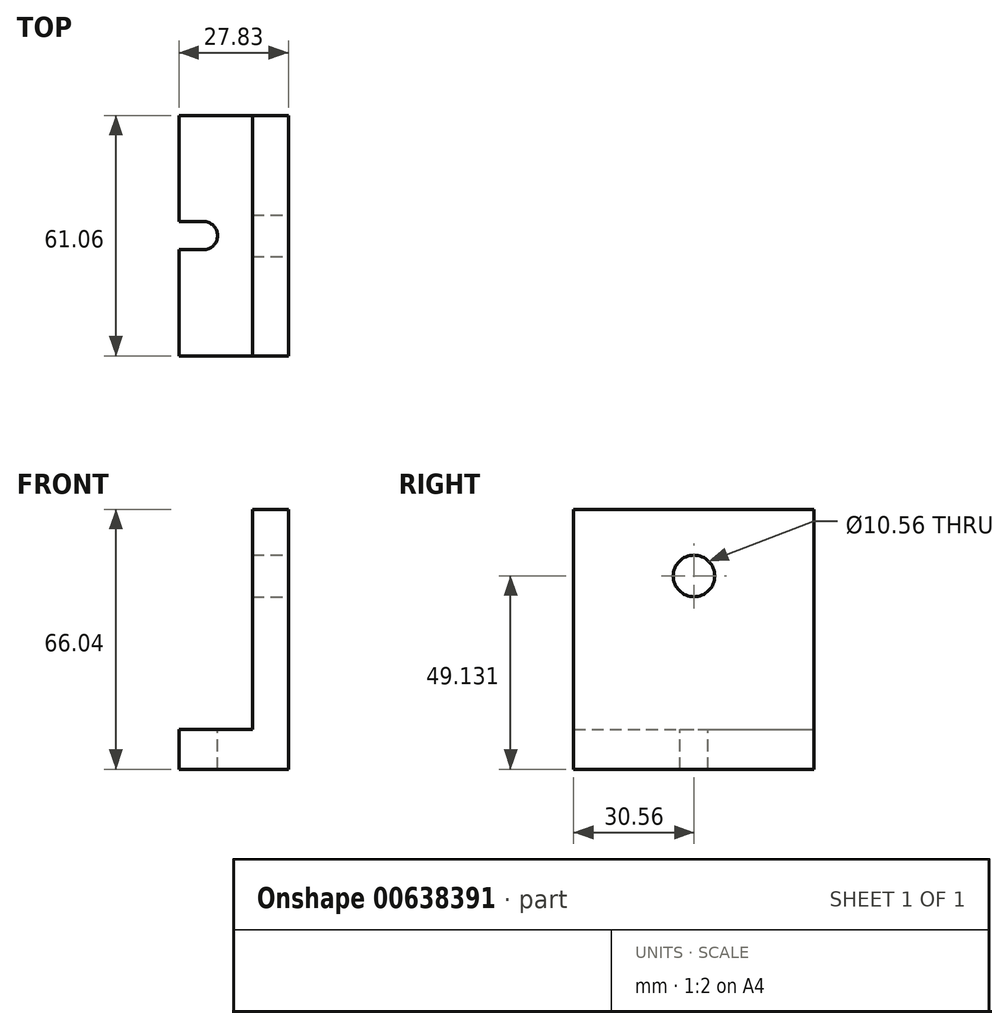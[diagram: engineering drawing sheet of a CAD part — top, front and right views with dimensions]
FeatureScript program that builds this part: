
annotation { "Feature Type Name" : "Feature", "Feature Type Description" : "" }
export const myFeature = defineFeature(function(context is Context, id is Id, definition is map)
    precondition{}
    {
        {
            var Q0;
            Q0=qCreatedBy(makeId("Top.planeOp"),FACE);
            var sketch = newSketch(context, id + "F0", { "sketchPlane" : qUnion([Q0])});
            skLineSegment(sketch, "E0.bottom", {"start": v(0, 0) * mm, "end": v(-18.7, 0) * mm});
            skLineSegment(sketch, "E0.top", {"start": v(0, 30.5) * mm, "end": v(-18.7, 30.5) * mm});
            skLineSegment(sketch, "E0.left", {"start": v(0, 0) * mm, "end": v(0, 30.5) * mm});
            skLineSegment(sketch, "E0.right", {"start": v(-18.7, 0) * mm, "end": v(-18.7, 30.5) * mm});
            skLineSegment(sketch, "E1.top", {"start": v(0, -30.56) * mm, "end": v(-18.7, -30.56) * mm});
            skLineSegment(sketch, "E1.left", {"start": v(0, 0) * mm, "end": v(0, -30.56) * mm});
            skLineSegment(sketch, "E1.right", {"start": v(-18.7, 0) * mm, "end": v(-18.7, -30.56) * mm});
            skLineSegment(sketch, "E2.bottom", {"start": v(0, 30.5) * mm, "end": v(9.13, 30.5) * mm});
            skLineSegment(sketch, "E2.top", {"start": v(0, -30.56) * mm, "end": v(9.13, -30.56) * mm});
            skLineSegment(sketch, "E2.left", {"start": v(0, 30.5) * mm, "end": v(0, -30.56) * mm});
            skLineSegment(sketch, "E2.right", {"start": v(9.13, 30.5) * mm, "end": v(9.13, -30.56) * mm});
            skSolve(sketch);
        }
        {
            var Q0;
            {var subQ3=sQuery(id+"F0.wireOp",EDGE,"E2.bottom");Q0=makeQuery(id+"F0.imprint","IMPRINT",FACE,{"disambiguationData":[TD([[makeQuery(id+"F0.imprint","IMPRINT",EDGE,{"derivedFrom":subQ3}),-1.0]])]});}
            extrude(context, id + "F1", {"entities" : qUnion([Q0]), "depth" : 66.04 * mm, "offsetDistance" : 25.4 * mm});
        }
        {
            var Q0;
            {var subQ0=sQuery(id+"F0.wireOp",EDGE,"E0.top");Q0=makeQuery(id+"F0.imprint","IMPRINT",FACE,{"disambiguationData":[TD([[makeQuery(id+"F0.imprint","IMPRINT",EDGE,{"derivedFrom":subQ0}),1.0]])]});}
            var Q1;
            {var subQ0=sQuery(id+"F0.wireOp",EDGE,"E0.bottom");Q1=makeQuery(id+"F0.imprint","IMPRINT",FACE,{"disambiguationData":[TD([[makeQuery(id+"F0.imprint","IMPRINT",EDGE,{"derivedFrom":subQ0}),1.0]])]});}
            extrude(context, id + "F2", {"entities" : qUnion([Q0, Q1]), "operationType" : NewBodyOperationType.ADD, "depth" : 10.16 * mm, "offsetDistance" : 25.4 * mm});
        }
        {
            var Q0;
            Q0=makeQuery(id+"F1.opExtrude","SWEPT_FACE",FACE,{"disambiguationData":[OSD([sQuery(id+"F0.wireOp",EDGE,"E2.right")])]});
            var sketch = newSketch(context, id + "F3", { "sketchPlane" : qUnion([Q0])});
            skCircle(sketch, "E3", {"center": v(0, 49.13) * mm, "radius": 5.28 * mm});
            skSolve(sketch);
        }
        {
            var Q0;
            Q0=makeQuery(id+"F3.imprint","IMPRINT",FACE,{"disambiguationData":[TD([[makeQuery(id+"F3.imprint","IMPRINT",EDGE,{"derivedFrom":sQuery(id+"F3.wireOp",EDGE,"E3")}),1.0]])]});
            extrude(context, id + "F4", {"entities" : qUnion([Q0]), "operationType" : NewBodyOperationType.REMOVE, "oppositeDirection" : true, "depth" : 25.4 * mm, "offsetDistance" : 25.4 * mm});
        }
        {
            var Q0;
            Q0=makeQuery(id+"F2.opExtrude","CAP_FACE",FACE,{"disambiguationData":[OSD([sQuery(id+"F0.wireOp",EDGE,"E0.top"),sQuery(id+"F0.wireOp",EDGE,"E0.right"),sQuery(id+"F0.wireOp",EDGE,"E1.top"),sQuery(id+"F0.wireOp",EDGE,"E1.right"),sQuery(id+"F0.wireOp",EDGE,"E2.left")])],"isStart":false});
            var sketch = newSketch(context, id + "F5", { "sketchPlane" : qUnion([Q0])});
            skCircle(sketch, "E4", {"center": v(-12.46, 0) * mm, "radius": 3.6 * mm});
            skLineSegment(sketch, "E5", {"start": v(-12.46, 0) * mm, "end": v(-12.46, 3.6) * mm});
            skLineSegment(sketch, "E6", {"start": v(-12.46, 0) * mm, "end": v(-12.46, -3.6) * mm});
            skLineSegment(sketch, "E7", {"start": v(-12.46, 3.6) * mm, "end": v(-18.7, 3.6) * mm});
            skLineSegment(sketch, "E8", {"start": v(-12.46, -3.6) * mm, "end": v(-19.35, -3.6) * mm});
            skSolve(sketch);
        }
        {
            var Q0;
            Q0 = qSketchRegion(id + "F5", true);
            var Q1;
            {var subQ0=sQuery(id+"F5.wireOp",EDGE,"E7");Q1=makeQuery(id+"F5.imprint","IMPRINT",FACE,{"disambiguationData":[TD([[makeQuery(id+"F5.imprint","IMPRINT",EDGE,{"derivedFrom":subQ0}),1.0]])]});}
            extrude(context, id + "F6", {"entities" : qUnion([Q0, Q1]), "operationType" : NewBodyOperationType.REMOVE, "oppositeDirection" : true, "depth" : 25.4 * mm, "offsetDistance" : 25.4 * mm});
        }
    });
